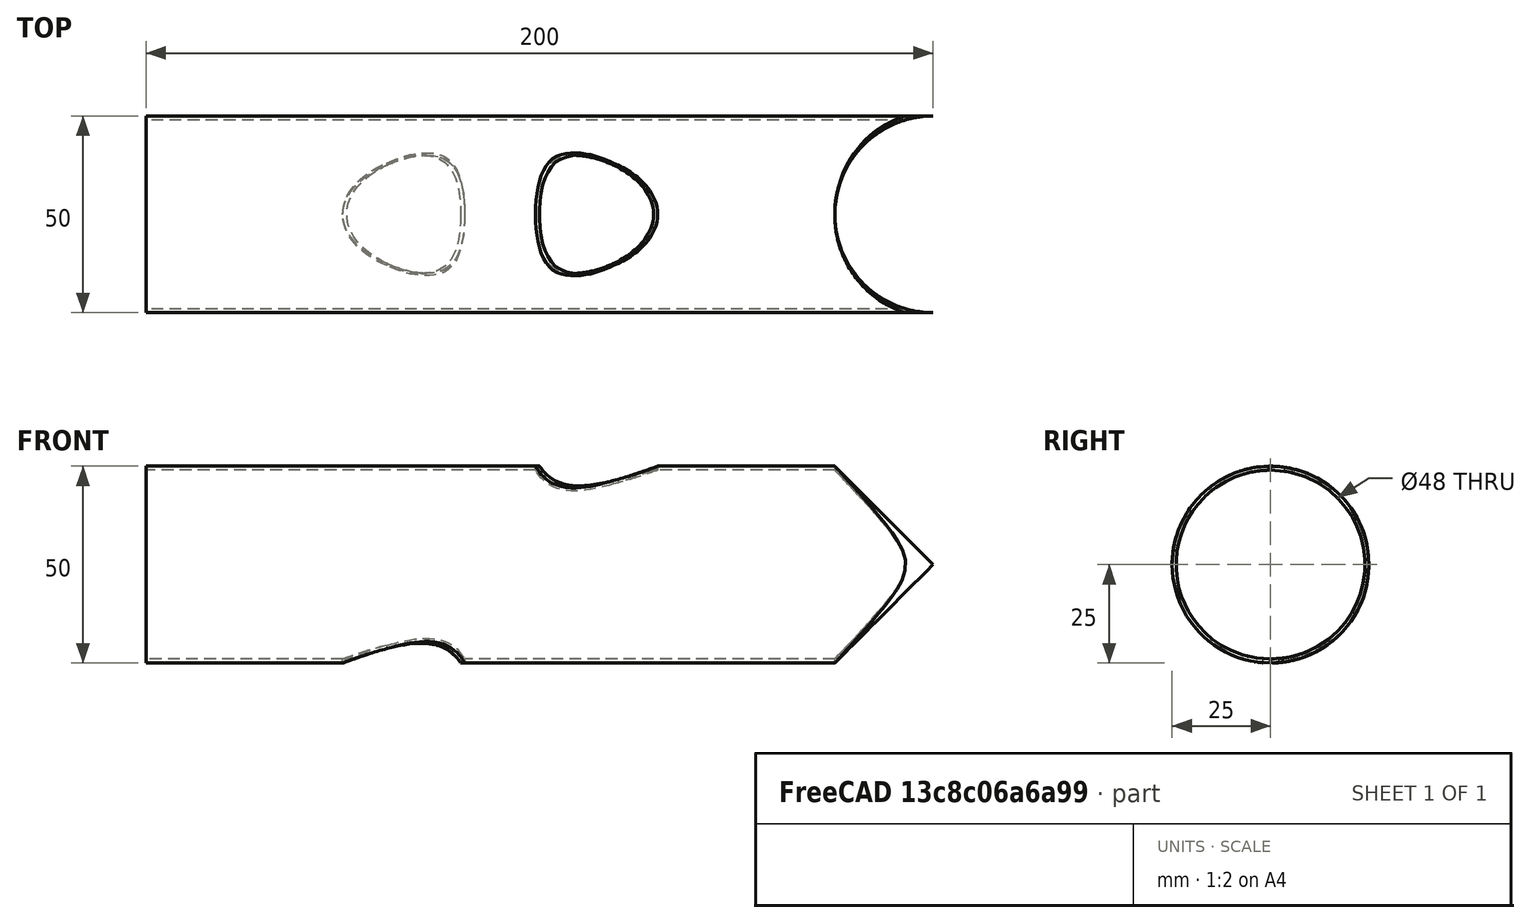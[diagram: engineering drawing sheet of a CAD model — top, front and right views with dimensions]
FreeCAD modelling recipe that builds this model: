
FCSTD DOCUMENT  (FreeCAD 0.20R25747 (Git))
Label: pipe_normalcut
License: All rights reserved
LicenseURL: http://en.wikipedia.org/wiki/All_rights_reserved
objects: Part::FeaturePython×4, App::Link×2, Part::Offset×2, Part::Cylinder×1, App::DocumentObjectGroup×1, Part::MultiCommon×1, Part::Feature×1, Part::Cut×1
note: 10 computed .brp shape members not serialized (recipe doc carries the construction recipe); baked Part::Feature solids carry a one-line shape summary decoded from their .brp

FEATURE [Part::Cylinder] Cylinder
  Angle = 360
  AttacherType = Attacher::AttachEngine3D
  FirstAngle = 45
  Height = 80
  Placement = pos=(-150,0,10) rot=(0,0,1;0rad)
  Radius = 15
  SecondAngle = 0
FEATURE [Part::FeaturePython] Tube  # WARN: FeaturePython — macro-defined, semantics opaque (R4)
  AttacherType = Attacher::AttachEngine3D
  Height = 100
  InnerRadius = 24
  OuterRadius = 25
FEATURE [Part::FeaturePython] Tube001  # WARN: FeaturePython — macro-defined, semantics opaque (R4)
  AttacherType = Attacher::AttachEngine3D
  Height = 200
  InnerRadius = 24
  OuterRadius = 25
  Placement = pos=(0,0,50) rot=(0.357407,-0.862856,-0.357407;1.71777rad)
FEATURE [App::DocumentObjectGroup] Group  label="Model"
FEATURE [Part::FeaturePython] Cutout  # WARN: FeaturePython — macro-defined, semantics opaque (R4)
  Base = -> Tube001
  Tolerance = 0
  Tool = -> Tube
FEATURE [Part::FeaturePython] Cutout001  # WARN: FeaturePython — macro-defined, semantics opaque (R4)
  Base = -> Cutout
  Tolerance = 0
  Tool = -> Cylinder
FEATURE [App::Link] Link  label="Cutout002"
  LinkTransform = true
  LinkedObject = -> Cutout001 [Face1]
FEATURE [App::Link] Link001  label="Cutout003"
  LinkTransform = true
  LinkedObject = -> Cutout001 [Face6]
FEATURE [Part::Offset] Offset
  Fill = true
  Intersection = false
  Join = 0
  Mode = 0
  SelfIntersection = false
  Source = -> Link
  Value = -1
FEATURE [Part::Offset] Offset001
  Fill = true
  Intersection = false
  Join = 0
  Mode = 0
  SelfIntersection = false
  Source = -> Link001
  Value = -1
FEATURE [Part::MultiCommon] Common
  Shapes = -> [Offset,Offset001]
FEATURE [Part::Feature] Common001
  shape: bbox 193 x 64.96 x 64.96 mm, 12 faces (baked)
FEATURE [Part::Cut] Cut  label="Highlight what has been remove"
  Base = -> Cutout001
  Tool = -> Common001
